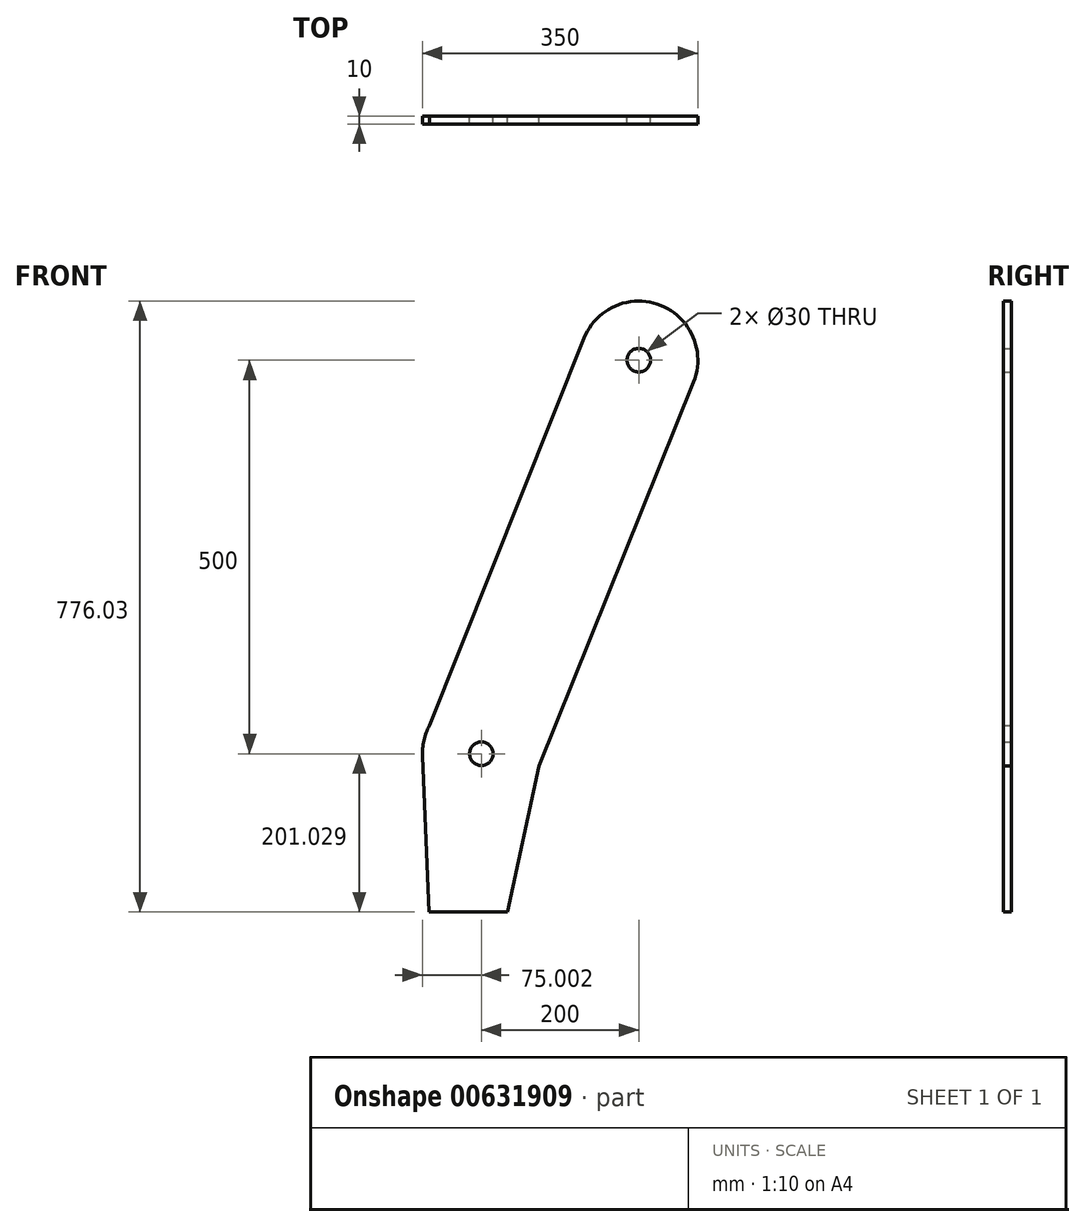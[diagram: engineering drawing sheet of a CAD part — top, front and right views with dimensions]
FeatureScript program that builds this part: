
annotation { "Feature Type Name" : "Feature", "Feature Type Description" : "" }
export const myFeature = defineFeature(function(context is Context, id is Id, definition is map)
    precondition{}
    {
        {
            var Q0;
            Q0=qCreatedBy(makeId("Front.planeOp"),FACE);
            var sketch = newSketch(context, id + "F0", { "sketchPlane" : qUnion([Q0])});
            skLineSegment(sketch, "E0", {"start": v(-148.47, -233.37) * mm, "end": v(-48.47, -233.37) * mm});
            skCircle(sketch, "E1", {"center": v(118.1, 467.66) * mm, "radius": 75 * mm});
            skCircle(sketch, "E2", {"center": v(118.1, 467.66) * mm, "radius": 15 * mm});
            skCircle(sketch, "E3", {"center": v(-81.9, -32.34) * mm, "radius": 75 * mm});
            skCircle(sketch, "E4", {"center": v(-81.9, -32.34) * mm, "radius": 15 * mm});
            skLineSegment(sketch, "E5", {"start": v(-148.47, -233.37) * mm, "end": v(-156.84, -35.51) * mm});
            skLineSegment(sketch, "E6", {"start": v(-147.8, 3.46) * mm, "end": v(48.43, 495.45) * mm});
            skLineSegment(sketch, "E7", {"start": v(-48.47, -233.37) * mm, "end": v(-8.59, -48.13) * mm});
            skLineSegment(sketch, "E8", {"start": v(-8.59, -48.13) * mm, "end": v(187.67, 439.66) * mm});
            skSolve(sketch);
        }
        {
            var Q0;
            Q0 = qSketchRegion(id + "F0", true);
            extrude(context, id + "F1", {"entities" : qUnion([Q0]), "depth" : 10 * mm, "offsetDistance" : 25 * mm});
        }
    });
